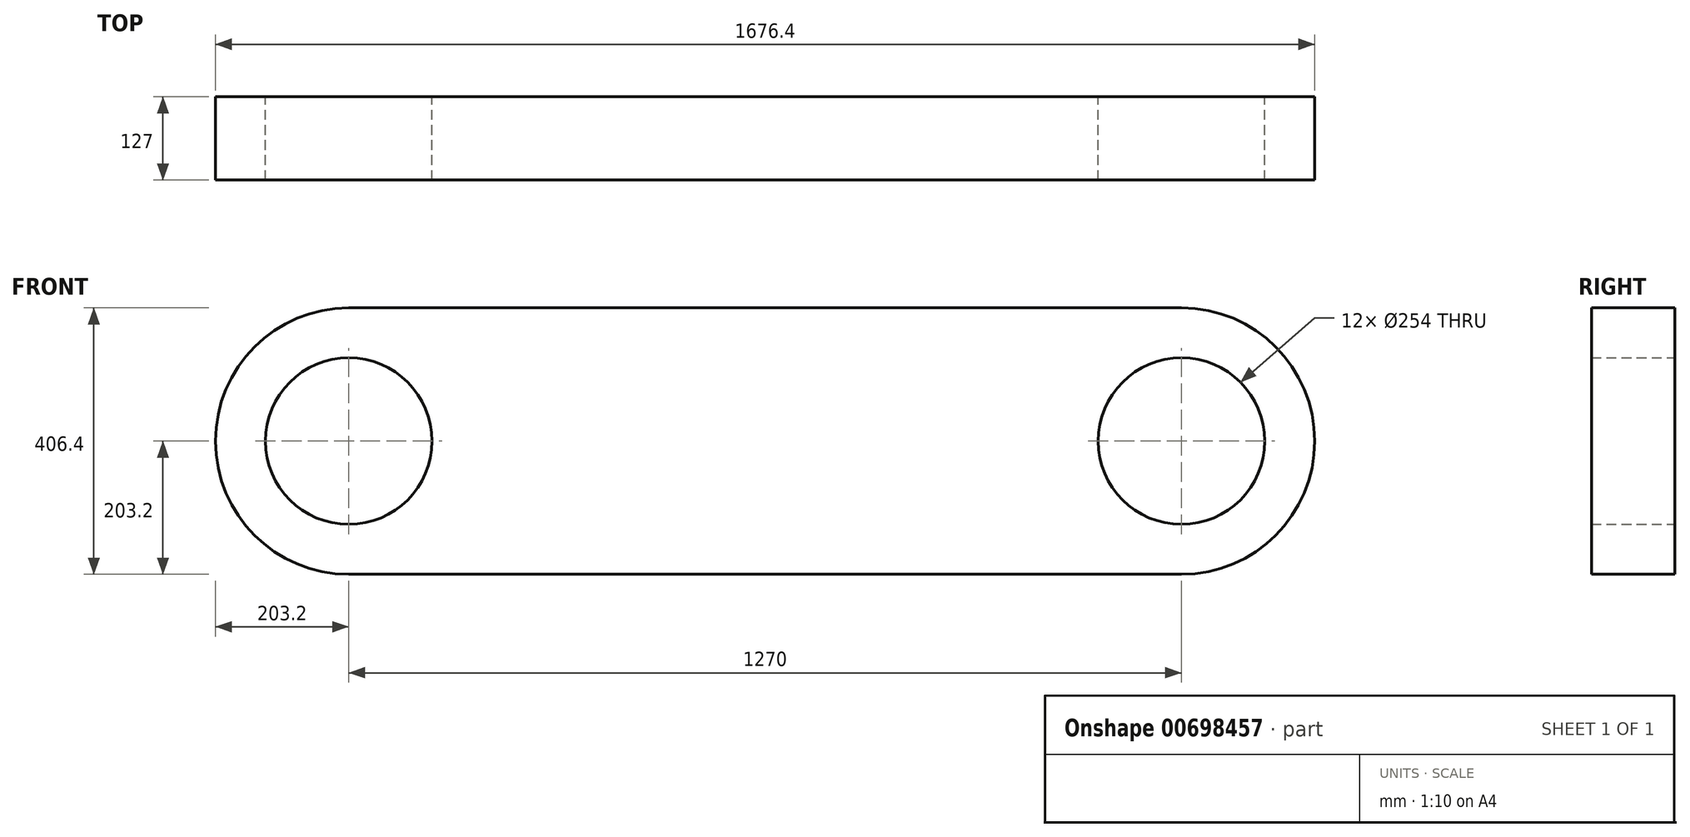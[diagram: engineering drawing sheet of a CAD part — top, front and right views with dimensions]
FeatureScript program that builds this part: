
annotation { "Feature Type Name" : "Feature", "Feature Type Description" : "" }
export const myFeature = defineFeature(function(context is Context, id is Id, definition is map)
    precondition{}
    {
        {
            var Q0;
            Q0=qCreatedBy(makeId("Front.planeOp"),FACE);
            var sketch = newSketch(context, id + "F0", { "sketchPlane" : qUnion([Q0])});
            skLineSegment(sketch, "E0.bottom", {"start": v(-635, 203.2) * mm, "end": v(635, 203.2) * mm});
            skLineSegment(sketch, "E0.top", {"start": v(-635, -203.2) * mm, "end": v(635, -203.2) * mm});
            skArc(sketch, "E1", {"start": v(-635, 203.2) * mm, "mid": v(-838.2, 0) * mm, "end": v(-635, -203.2) * mm});
            skArc(sketch, "E2", {"start": v(635, -203.2) * mm, "mid": v(838.2, 0) * mm, "end": v(635, 203.2) * mm});
            skCircle(sketch, "E3", {"center": v(635, 0) * mm, "radius": 127 * mm});
            skCircle(sketch, "E4", {"center": v(-635, 0) * mm, "radius": 127 * mm});
            skSolve(sketch);
        }
        {
            var Q0;
            Q0=qSketchRegion(id+"F0",true);
            extrude(context, id + "F1", {"entities" : qUnion([Q0]), "endBound" : BoundingType.SYMMETRIC, "depth" : 127 * mm, "offsetDistance" : 25.4 * mm});
        }
    });
